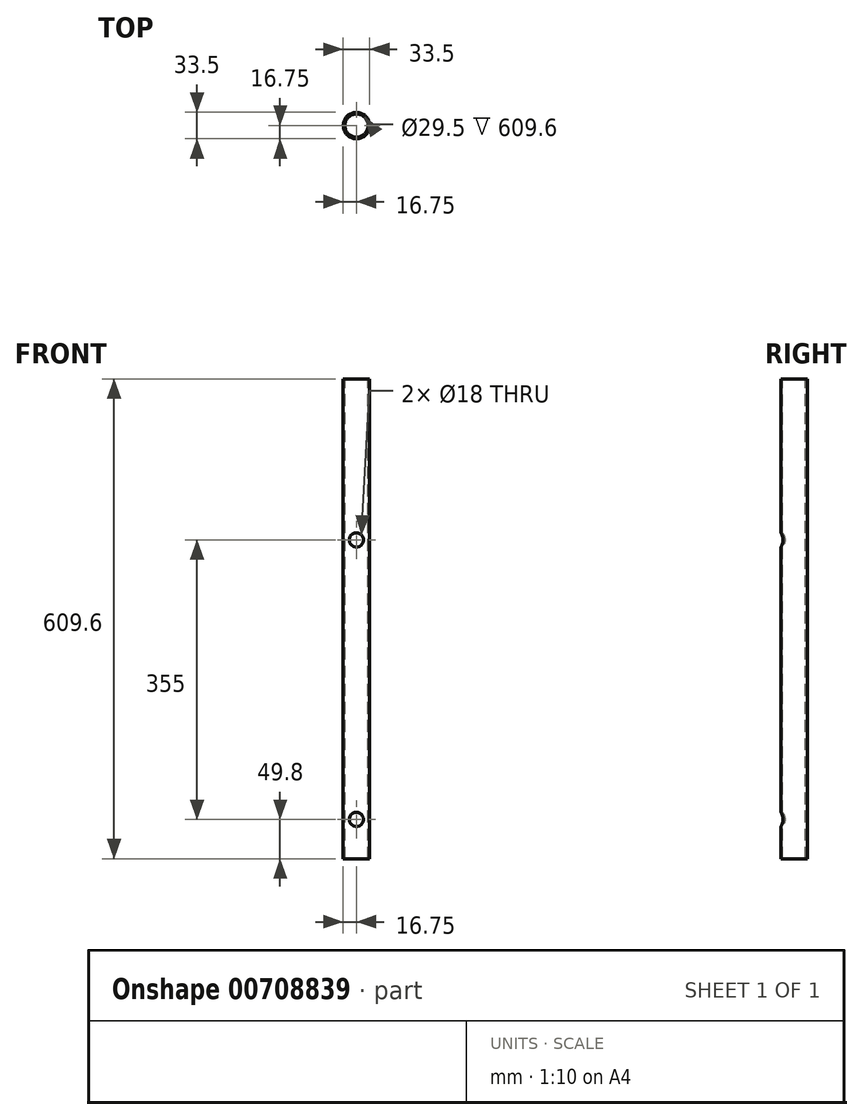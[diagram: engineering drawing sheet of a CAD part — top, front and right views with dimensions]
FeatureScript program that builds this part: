
annotation { "Feature Type Name" : "Feature", "Feature Type Description" : "" }
export const myFeature = defineFeature(function(context is Context, id is Id, definition is map)
    precondition{}
    {
        {
            var Q0;
            Q0=qCreatedBy(makeId("Top.planeOp"),FACE);
            var sketch = newSketch(context, id + "F0", { "sketchPlane" : qUnion([Q0])});
            skCircle(sketch, "E0", {"center": v(0, 0) * mm, "radius": 16.75 * mm});
            skSolve(sketch);
        }
        {
            var Q0;
            Q0=makeQuery(id+"F0.imprint","IMPRINT",FACE,{"disambiguationData":[TD([[makeQuery(id+"F0.imprint","IMPRINT",EDGE,{"derivedFrom":sQuery(id+"F0.wireOp",EDGE,"E0")}),1.0]])]});
            extrude(context, id + "F1", {"entities" : qUnion([Q0]), "oppositeDirection" : true, "depth" : 609.6 * mm, "offsetDistance" : 25 * mm});
        }
        {
            var Q0;
            Q0=qCreatedBy(makeId("Top.planeOp"),FACE);
            var sketch = newSketch(context, id + "F2", { "sketchPlane" : qUnion([Q0])});
            skCircle(sketch, "E1", {"center": v(0, 0) * mm, "radius": 14.75 * mm});
            skSolve(sketch);
        }
        {
            var Q0;
            Q0 = qSketchRegion(id + "F2", true);
            var Q1;
            Q1=makeQuery(id+"F2.imprint","IMPRINT",FACE,{"disambiguationData":[TD([[makeQuery(id+"F2.imprint","IMPRINT",EDGE,{"derivedFrom":sQuery(id+"F2.wireOp",EDGE,"E1")}),1.0]])]});
            extrude(context, id + "F3", {"entities" : qUnion([Q0, Q1]), "operationType" : NewBodyOperationType.REMOVE, "oppositeDirection" : true, "depth" : 609.6 * mm, "offsetDistance" : 25 * mm});
        }
        {
            var Q0;
            Q0=qCreatedBy(makeId("Front.planeOp"),FACE);
            var sketch = newSketch(context, id + "F4", { "sketchPlane" : qUnion([Q0])});
            skCircle(sketch, "E2", {"center": v(0, -204.8) * mm, "radius": 9 * mm});
            skSolve(sketch);
        }
        {
            var Q0;
            Q0=qCreatedBy(makeId("Front.planeOp"),FACE);
            var sketch = newSketch(context, id + "F5", { "sketchPlane" : qUnion([Q0])});
            skCircle(sketch, "E3", {"center": v(0, -559.8) * mm, "radius": 9 * mm});
            skSolve(sketch);
        }
        {
            var Q0;
            Q0 = qSketchRegion(id + "F4", true);
            extrude(context, id + "F6", {"entities" : qUnion([Q0]), "operationType" : NewBodyOperationType.REMOVE, "depth" : 25 * mm, "offsetDistance" : 25 * mm});
        }
        {
            var Q0;
            Q0 = qSketchRegion(id + "F5", true);
            extrude(context, id + "F7", {"entities" : qUnion([Q0]), "operationType" : NewBodyOperationType.REMOVE, "depth" : 25 * mm, "offsetDistance" : 25 * mm});
        }
        {
            var Q0;
            Q0=qCreatedBy(makeId("Front.planeOp"),FACE);
            cPlane(context, id + "F8", {"entities" : qUnion([Q0]), "cplaneType" : CPlaneType.OFFSET, "offset" : 16.75 * mm, "width" : 150 * mm, "height" : 150 * mm});
        }
    });
